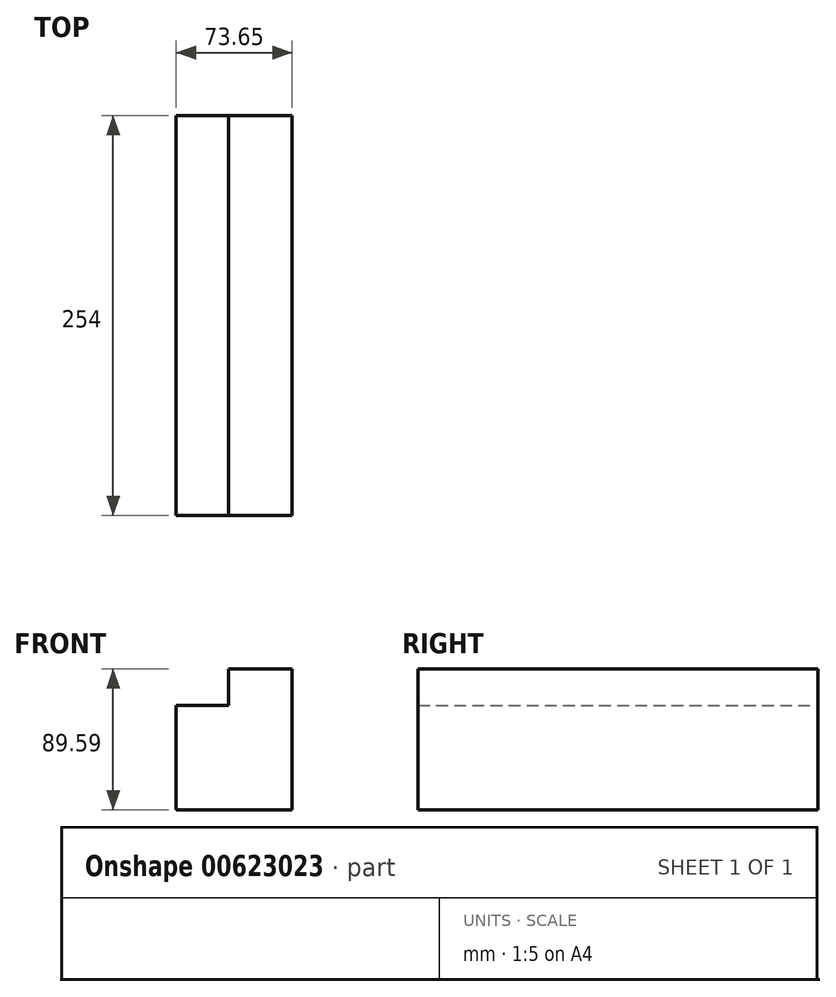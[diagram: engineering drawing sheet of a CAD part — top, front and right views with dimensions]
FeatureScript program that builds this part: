
annotation { "Feature Type Name" : "Feature", "Feature Type Description" : "" }
export const myFeature = defineFeature(function(context is Context, id is Id, definition is map)
    precondition{}
    {
        {
            var Q0;
            Q0=qCreatedBy(makeId("Front.planeOp"),FACE);
            var sketch = newSketch(context, id + "F0", { "sketchPlane" : qUnion([Q0])});
            skLineSegment(sketch, "E0.bottom", {"start": v(-40.28, 49.31) * mm, "end": v(0, 49.31) * mm});
            skLineSegment(sketch, "E0.top", {"start": v(-40.28, -40.28) * mm, "end": v(0, -40.28) * mm});
            skLineSegment(sketch, "E0.left", {"start": v(-40.28, 49.31) * mm, "end": v(-40.28, -40.28) * mm});
            skLineSegment(sketch, "E0.right", {"start": v(0, 49.31) * mm, "end": v(0, -40.28) * mm});
            skLineSegment(sketch, "E1.bottom", {"start": v(-40.28, 26.09) * mm, "end": v(-73.65, 26.09) * mm});
            skLineSegment(sketch, "E1.top", {"start": v(-40.28, -40.28) * mm, "end": v(-73.65, -40.28) * mm});
            skLineSegment(sketch, "E1.left", {"start": v(-40.28, 26.09) * mm, "end": v(-40.28, -40.28) * mm});
            skLineSegment(sketch, "E1.right", {"start": v(-73.65, 26.09) * mm, "end": v(-73.65, -40.28) * mm});
            skSolve(sketch);
        }
        {
            var Q0;
            Q0 = qSketchRegion(id + "F0", true);
            extrude(context, id + "F1", {"entities" : qUnion([Q0]), "depth" : 254 * mm, "offsetDistance" : 25.4 * mm});
        }
    });
